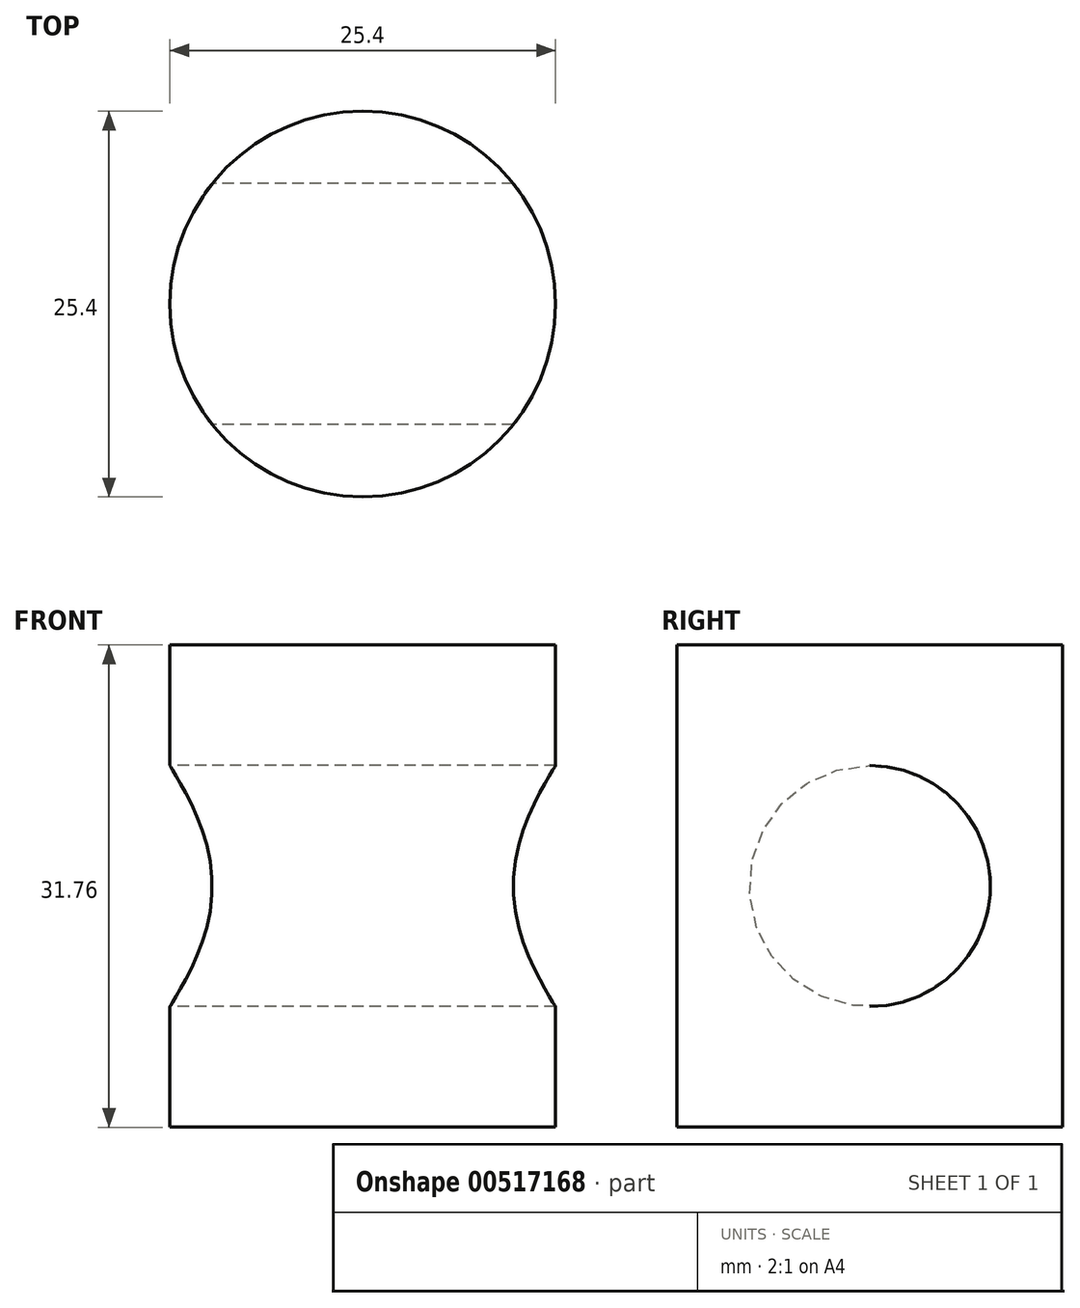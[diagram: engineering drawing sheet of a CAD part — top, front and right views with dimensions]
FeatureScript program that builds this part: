
annotation { "Feature Type Name" : "Feature", "Feature Type Description" : "" }
export const myFeature = defineFeature(function(context is Context, id is Id, definition is map)
    precondition{}
    {
        {
            var Q0;
            Q0=qCreatedBy(makeId("Top.planeOp"),FACE);
            var sketch = newSketch(context, id + "F0", { "sketchPlane" : qUnion([Q0])});
            skCircle(sketch, "E0", {"center": v(0, 0) * mm, "radius": 12.7 * mm});
            skSolve(sketch);
        }
        {
            var Q0;
            Q0=makeQuery(id+"F0.imprint","IMPRINT",FACE,{"disambiguationData":[TD([[makeQuery(id+"F0.imprint","IMPRINT",EDGE,{"derivedFrom":sQuery(id+"F0.wireOp",EDGE,"E0")}),1.0]])]});
            extrude(context, id + "F1", {"entities" : qUnion([Q0]), "endBound" : BoundingType.SYMMETRIC, "depth" : 31.75 * mm, "offsetDistance" : 25.4 * mm});
        }
        {
            var Q0;
            Q0=qCreatedBy(makeId("Right.planeOp"),FACE);
            var sketch = newSketch(context, id + "F2", { "sketchPlane" : qUnion([Q0])});
            skCircle(sketch, "E1", {"center": v(0, 0) * mm, "radius": 7.94 * mm});
            skSolve(sketch);
        }
        {
            var Q0;
            Q0 = qSketchRegion(id + "F2", true);
            extrude(context, id + "F3", {"entities" : qUnion([Q0]), "operationType" : NewBodyOperationType.REMOVE, "endBound" : BoundingType.SYMMETRIC, "depth" : 25.4 * mm, "offsetDistance" : 25.4 * mm});
        }
    });
